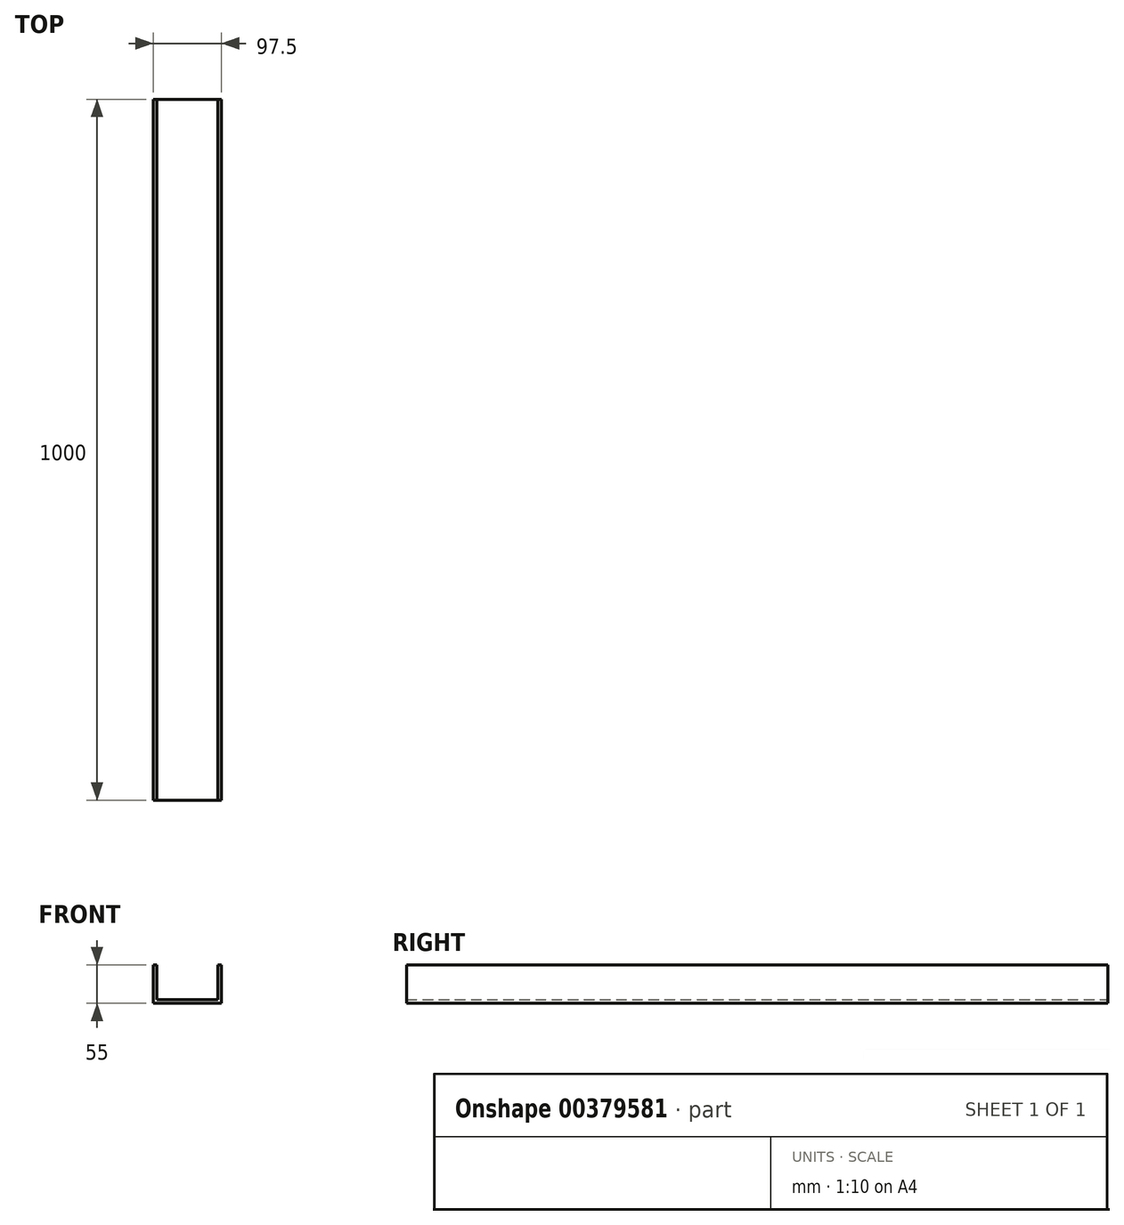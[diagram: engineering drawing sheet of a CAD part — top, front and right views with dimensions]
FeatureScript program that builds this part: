
annotation { "Feature Type Name" : "Feature", "Feature Type Description" : "" }
export const myFeature = defineFeature(function(context is Context, id is Id, definition is map)
    precondition{}
    {
        {
            var Q0;
            Q0=qCreatedBy(makeId("Front.planeOp"),FACE);
            var sketch = newSketch(context, id + "F0", { "sketchPlane" : qUnion([Q0])});
            skLineSegment(sketch, "E0.left", {"start": v(45, 19.33) * mm, "end": v(45, -15.67) * mm});
            skLineSegment(sketch, "E0.right", {"start": v(-42.5, 19.33) * mm, "end": v(-42.5, -15.67) * mm});
            skLineSegment(sketch, "E1.bottom", {"start": v(-42.5, 19.33) * mm, "end": v(-47.5, 19.33) * mm});
            skLineSegment(sketch, "E1.top", {"start": v(-42.5, -30.67) * mm, "end": v(-47.5, -30.67) * mm});
            skLineSegment(sketch, "E1.left", {"start": v(-42.5, 19.33) * mm, "end": v(-42.5, -30.67) * mm});
            skLineSegment(sketch, "E1.right", {"start": v(-47.5, 19.33) * mm, "end": v(-47.5, -30.67) * mm});
            skLineSegment(sketch, "E2.bottom", {"start": v(45, 19.33) * mm, "end": v(50, 19.33) * mm});
            skLineSegment(sketch, "E2.top", {"start": v(45, -30.67) * mm, "end": v(50, -30.67) * mm});
            skLineSegment(sketch, "E2.left", {"start": v(45, 19.33) * mm, "end": v(45, -30.67) * mm});
            skLineSegment(sketch, "E2.right", {"start": v(50, 19.33) * mm, "end": v(50, -30.67) * mm});
            skLineSegment(sketch, "E3.bottom", {"start": v(-47.5, -30.67) * mm, "end": v(50, -30.67) * mm});
            skLineSegment(sketch, "E3.top", {"start": v(-47.5, -35.67) * mm, "end": v(50, -35.67) * mm});
            skLineSegment(sketch, "E3.left", {"start": v(-47.5, -30.67) * mm, "end": v(-47.5, -35.67) * mm});
            skLineSegment(sketch, "E3.right", {"start": v(50, -30.67) * mm, "end": v(50, -35.67) * mm});
            skLineSegment(sketch, "E4.bottom", {"start": v(-42.5, -30.67) * mm, "end": v(-38.75, -30.67) * mm});
            skLineSegment(sketch, "E4.top", {"start": v(-42.5, -28.17) * mm, "end": v(-38.75, -28.17) * mm});
            skLineSegment(sketch, "E4.left", {"start": v(-42.5, -30.67) * mm, "end": v(-42.5, -28.17) * mm});
            skLineSegment(sketch, "E4.right", {"start": v(-38.75, -30.67) * mm, "end": v(-38.75, -28.17) * mm});
            skLineSegment(sketch, "E5.bottom", {"start": v(45, -30.67) * mm, "end": v(41.25, -30.67) * mm});
            skLineSegment(sketch, "E5.top", {"start": v(45, -28.17) * mm, "end": v(41.25, -28.17) * mm});
            skLineSegment(sketch, "E5.left", {"start": v(45, -30.67) * mm, "end": v(45, -28.17) * mm});
            skLineSegment(sketch, "E5.right", {"start": v(41.25, -30.67) * mm, "end": v(41.25, -28.17) * mm});
            skLineSegment(sketch, "E6.bottom", {"start": v(-13.75, -30.67) * mm, "end": v(16.25, -30.67) * mm});
            skLineSegment(sketch, "E6.top", {"start": v(-13.75, -28.17) * mm, "end": v(16.25, -28.17) * mm});
            skLineSegment(sketch, "E6.left", {"start": v(-13.75, -30.67) * mm, "end": v(-13.75, -28.17) * mm});
            skLineSegment(sketch, "E6.right", {"start": v(16.25, -30.67) * mm, "end": v(16.25, -28.17) * mm});
            skSolve(sketch);
        }
        {
            var Q0;
            {var subQ4=sQuery(id+"F0.wireOp",EDGE,"E1.bottom");Q0=makeQuery(id+"F0.imprint","IMPRINT",FACE,{"disambiguationData":[TD([[makeQuery(id+"F0.imprint","IMPRINT",EDGE,{"derivedFrom":subQ4}),1.0]])]});}
            var Q1;
            Q1=makeQuery(id+"F0.imprint","IMPRINT",FACE,{"disambiguationData":[TD([[makeQuery(id+"F0.imprint","IMPRINT",EDGE,{"derivedFrom":sQuery(id+"F0.wireOp",EDGE,"E3.top")}),1.0]])]});
            var Q2;
            {var subQ4=sQuery(id+"F0.wireOp",EDGE,"E2.bottom");Q2=makeQuery(id+"F0.imprint","IMPRINT",FACE,{"disambiguationData":[TD([[makeQuery(id+"F0.imprint","IMPRINT",EDGE,{"derivedFrom":subQ4}),-1.0]])]});}
            var Q3;
            Q3=makeQuery(id+"F0.imprint","IMPRINT",FACE,{"disambiguationData":[TD([[makeQuery(id+"F0.imprint","IMPRINT",EDGE,{"derivedFrom":sQuery(id+"F0.wireOp",EDGE,"E5.bottom")}),-1.0]])]});
            var Q4;
            Q4=makeQuery(id+"F0.imprint","IMPRINT",FACE,{"disambiguationData":[TD([[makeQuery(id+"F0.imprint","IMPRINT",EDGE,{"derivedFrom":sQuery(id+"F0.wireOp",EDGE,"E6.bottom")}),1.0]])]});
            var Q5;
            Q5=makeQuery(id+"F0.imprint","IMPRINT",FACE,{"disambiguationData":[TD([[makeQuery(id+"F0.imprint","IMPRINT",EDGE,{"derivedFrom":sQuery(id+"F0.wireOp",EDGE,"E4.bottom")}),1.0]])]});
            extrude(context, id + "F1", {"entities" : qUnion([Q0, Q1, Q2, Q3, Q4, Q5]), "depth" : 1000 * mm});
        }
    });
